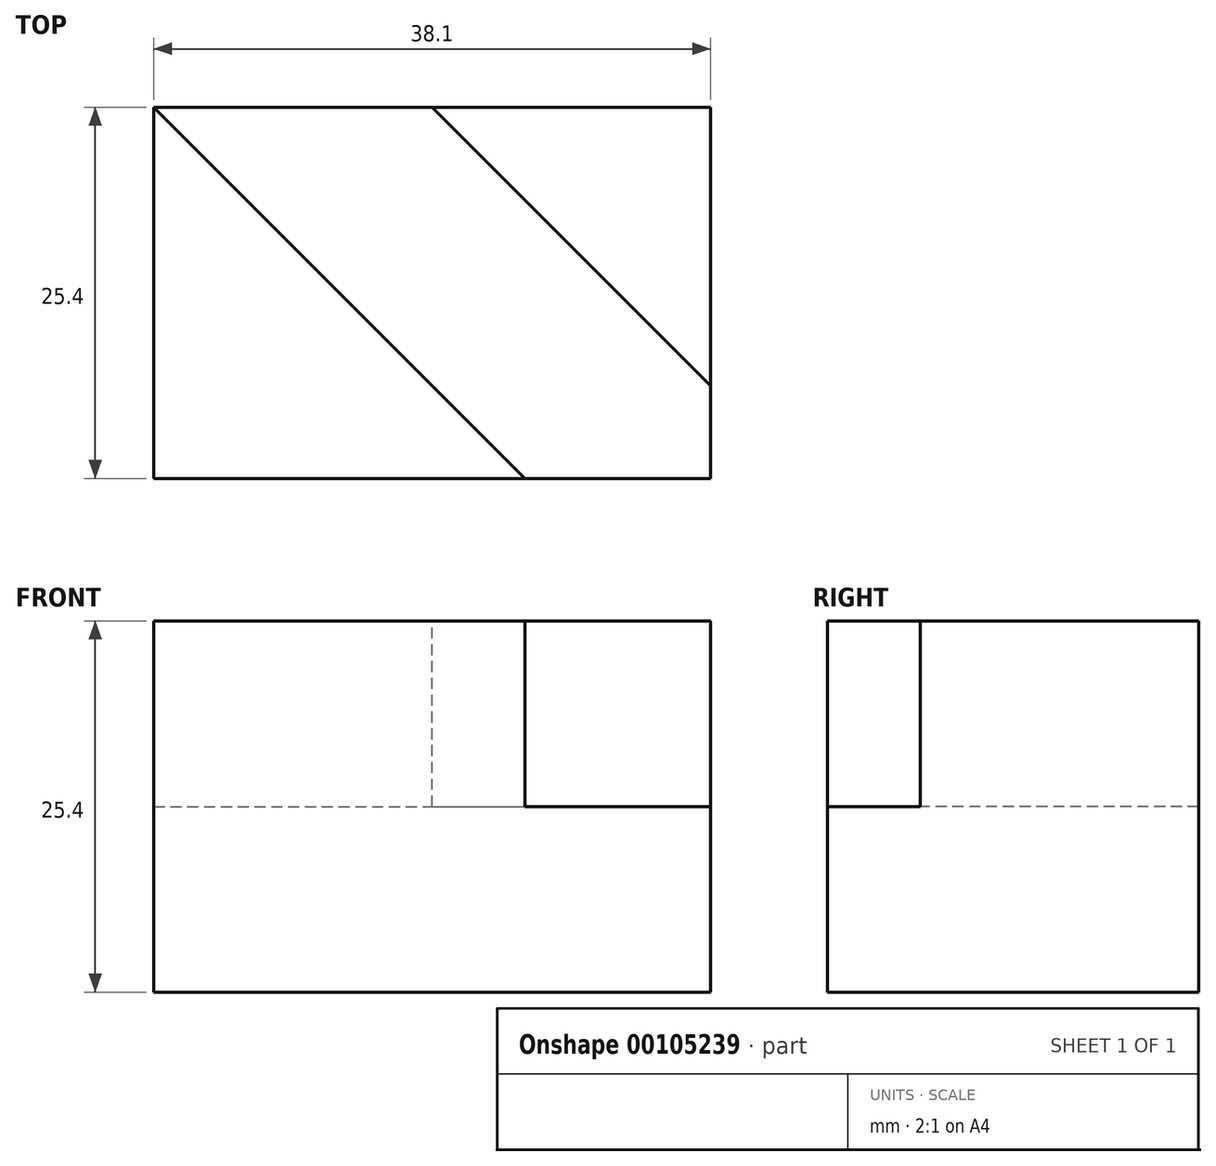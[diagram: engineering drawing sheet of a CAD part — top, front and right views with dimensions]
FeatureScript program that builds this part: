
annotation { "Feature Type Name" : "Feature", "Feature Type Description" : "" }
export const myFeature = defineFeature(function(context is Context, id is Id, definition is map)
    precondition{}
    {
        {
            var Q0;
            Q0=qCreatedBy(makeId("Front.planeOp"),FACE);
            var sketch = newSketch(context, id + "F0", { "sketchPlane" : qUnion([Q0])});
            skLineSegment(sketch, "E0.bottom", {"start": v(0, 0) * mm, "end": v(38.1, 0) * mm});
            skLineSegment(sketch, "E0.top", {"start": v(0, 25.4) * mm, "end": v(38.1, 25.4) * mm});
            skLineSegment(sketch, "E0.left", {"start": v(0, 0) * mm, "end": v(0, 25.4) * mm});
            skLineSegment(sketch, "E0.right", {"start": v(38.1, 0) * mm, "end": v(38.1, 25.4) * mm});
            skSolve(sketch);
        }
        {
            var Q0;
            Q0 = qSketchRegion(id + "F0", true);
            extrude(context, id + "F1", {"entities" : qUnion([Q0]), "depth" : 25.4 * mm});
        }
        {
            var Q0;
            Q0=makeQuery(id+"F1.opExtrude","SWEPT_FACE",FACE,{"disambiguationData":[OSD([sQuery(id+"F0.wireOp",EDGE,"E0.top")])]});
            var sketch = newSketch(context, id + "F2", { "sketchPlane" : qUnion([Q0])});
            skLineSegment(sketch, "E1", {"start": v(19.05, 0) * mm, "end": v(38.1, -19.05) * mm});
            skLineSegment(sketch, "E2", {"start": v(38.1, -19.05) * mm, "end": v(38.1, 0) * mm});
            skLineSegment(sketch, "E3", {"start": v(38.1, 0) * mm, "end": v(19.05, 0) * mm});
            skLineSegment(sketch, "E4", {"start": v(0, 0) * mm, "end": v(25.4, -25.4) * mm});
            skLineSegment(sketch, "E5", {"start": v(0, 0) * mm, "end": v(0, -25.4) * mm});
            skLineSegment(sketch, "E6", {"start": v(0, -25.4) * mm, "end": v(25.4, -25.4) * mm});
            skSolve(sketch);
        }
        {
            var Q0;
            {var subQ3=sQuery(id+"F2.wireOp",EDGE,"E1");Q0=makeQuery(id+"F2.imprint","IMPRINT",FACE,{"disambiguationData":[TD([[makeQuery(id+"F2.imprint","IMPRINT",EDGE,{"derivedFrom":subQ3}),-1.0]])]});}
            extrude(context, id + "F3", {"entities" : qUnion([Q0]), "operationType" : NewBodyOperationType.REMOVE, "oppositeDirection" : true, "depth" : 12.7 * mm});
        }
    });
